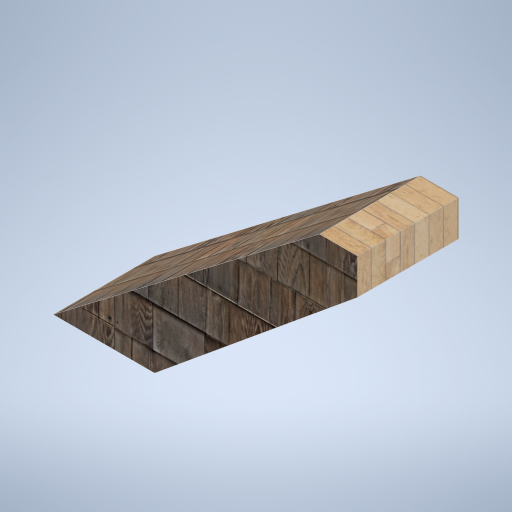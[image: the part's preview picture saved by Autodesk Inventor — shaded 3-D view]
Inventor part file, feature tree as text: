
AUTODESK INVENTOR PART (.ipt)
format: ipt  version: 2024.2 (Build 282272000, 272)  size: 327,680 bytes
history: native  units: in
note: dims shown in document units (in); Inventor stores cm internally (conversion verified against a paired STEP export)
features: other x3, sketch x1
ambient origin geometry x8: Origin, YZ Plane, XZ Plane, XY Plane, X Axis, Y Axis, Z Axis, Center Point
bodies: Body1 (feature_tree)
feature tree (4):
  other  "frame_rib_02.ipt"
  other  "Solid3::frame_rib_02.ipt"
  other  "TaggingFeature1"
  sketch  "Sketch1"  dims[d0=0.3937in]
